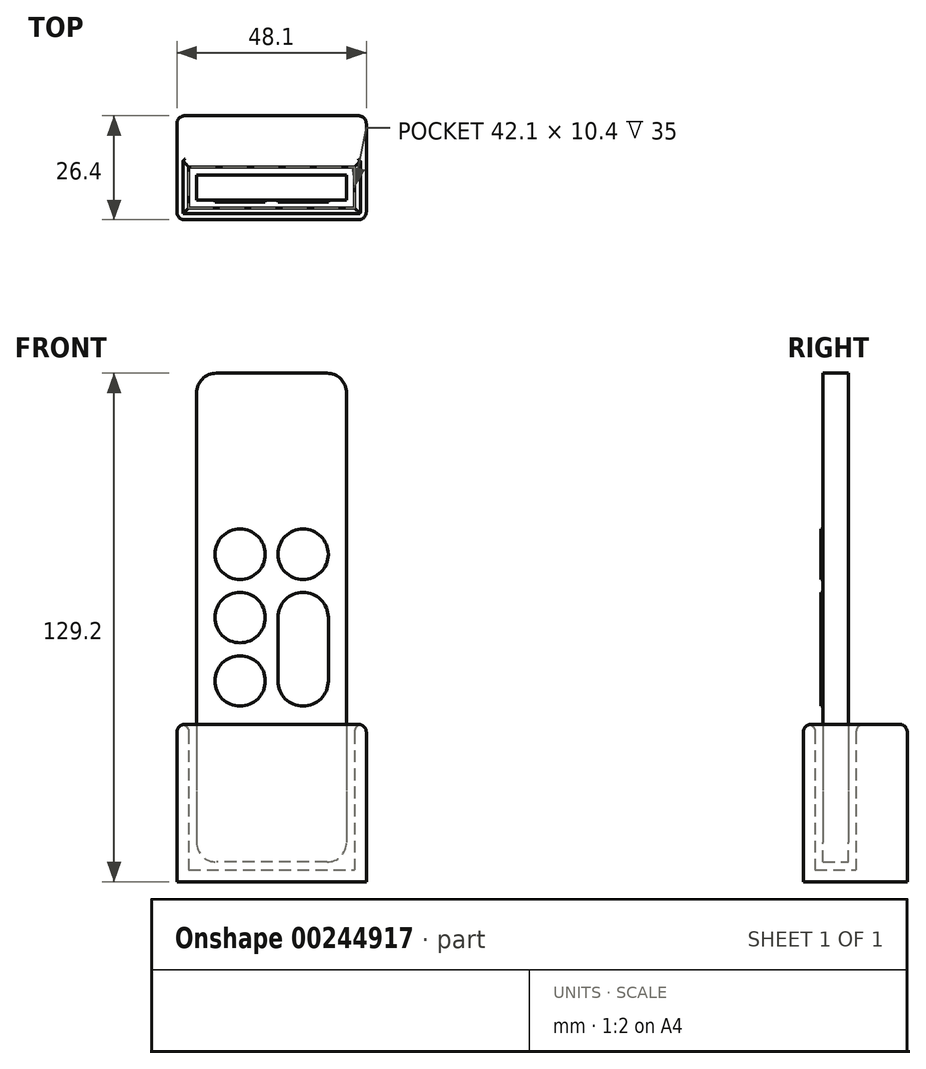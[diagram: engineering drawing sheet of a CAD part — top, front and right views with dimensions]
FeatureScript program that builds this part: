
annotation { "Feature Type Name" : "Feature", "Feature Type Description" : "" }
export const myFeature = defineFeature(function(context is Context, id is Id, definition is map)
    precondition{}
    {
        {
            var Q0;
            Q0=qCreatedBy(makeId("Front.planeOp"),FACE);
            var sketch = newSketch(context, id + "F0", { "sketchPlane" : qUnion([Q0])});
            skLineSegment(sketch, "E0.bottom", {"start": v(14.05, 62.1) * mm, "end": v(-14.05, 62.1) * mm});
            skLineSegment(sketch, "E0.top", {"start": v(14.05, -62.1) * mm, "end": v(-14.05, -62.1) * mm});
            skLineSegment(sketch, "E0.left", {"start": v(19.05, 57.1) * mm, "end": v(19.05, -57.1) * mm});
            skLineSegment(sketch, "E0.right", {"start": v(-19.05, 57.1) * mm, "end": v(-19.05, -57.1) * mm});
            skPoint(sketch, "E0.middle", {"position": v(0, 0) * mm});
            skPoint(sketch, "E1.visualSharp", {"position": v(19.05, 62.1) * mm});
            skArc(sketch, "E1.filletArc", {"start": v(19.05, 57.1) * mm, "mid": v(17.59, 60.64) * mm, "end": v(14.05, 62.1) * mm});
            skPoint(sketch, "E2.visualSharp", {"position": v(19.05, -62.1) * mm});
            skArc(sketch, "E2.filletArc", {"start": v(14.05, -62.1) * mm, "mid": v(17.59, -60.64) * mm, "end": v(19.05, -57.1) * mm});
            skPoint(sketch, "E3.visualSharp", {"position": v(-19.05, -62.1) * mm});
            skArc(sketch, "E3.filletArc", {"start": v(-19.05, -57.1) * mm, "mid": v(-17.59, -60.64) * mm, "end": v(-14.05, -62.1) * mm});
            skPoint(sketch, "E4.visualSharp", {"position": v(-19.05, 62.1) * mm});
            skArc(sketch, "E4.filletArc", {"start": v(-14.05, 62.1) * mm, "mid": v(-17.59, 60.64) * mm, "end": v(-19.05, 57.1) * mm});
            skSolve(sketch);
        }
        {
            var Q0;
            Q0 = qSketchRegion(id + "F0", true);
            extrude(context, id + "F1", {"entities" : qUnion([Q0]), "depth" : 6.4 * mm});
        }
        {
            var Q0;
            Q0=makeQuery(id+"F1.opExtrude","CAP_FACE",FACE,{"disambiguationData":[OSD([sQuery(id+"F0.wireOp",EDGE,"E0.bottom"),sQuery(id+"F0.wireOp",EDGE,"E0.top"),sQuery(id+"F0.wireOp",EDGE,"E0.left"),sQuery(id+"F0.wireOp",EDGE,"E0.right"),sQuery(id+"F0.wireOp",EDGE,"E1.filletArc"),sQuery(id+"F0.wireOp",EDGE,"E2.filletArc"),sQuery(id+"F0.wireOp",EDGE,"E3.filletArc"),sQuery(id+"F0.wireOp",EDGE,"E4.filletArc")])],"isStart":false});
            var sketch = newSketch(context, id + "F2", { "sketchPlane" : qUnion([Q0])});
            skLineSegment(sketch, "E5", {"start": v(0, 62.1) * mm, "end": v(0, -62.1) * mm, "construction": true});
            skLineSegment(sketch, "E6", {"start": v(8, 62.1) * mm, "end": v(8, -62.1) * mm, "construction": true});
            skLineSegment(sketch, "E7", {"start": v(-19.05, 0) * mm, "end": v(19.05, 0) * mm, "construction": true});
            skLineSegment(sketch, "E8", {"start": v(-19.05, 16.1) * mm, "end": v(19.05, 16.1) * mm, "construction": true});
            skCircle(sketch, "E9", {"center": v(8, 0) * mm, "radius": 6.4 * mm});
            skCircle(sketch, "E10", {"center": v(8, 16.1) * mm, "radius": 6.4 * mm});
            skCircle(sketch, "E11.MirrorC", {"center": v(8, -16.1) * mm, "radius": 6.4 * mm});
            skCircle(sketch, "E12.MirrorC", {"center": v(-8, 16.1) * mm, "radius": 6.4 * mm});
            skCircle(sketch, "E13.MirrorC", {"center": v(-8, 0) * mm, "radius": 6.4 * mm});
            skCircle(sketch, "E14.MirrorC", {"center": v(-8, -16.1) * mm, "radius": 6.4 * mm});
            skLineSegment(sketch, "E15", {"start": v(1.6, 0) * mm, "end": v(1.6, -16.1) * mm});
            skLineSegment(sketch, "E16", {"start": v(14.4, 0) * mm, "end": v(14.4, -16.1) * mm});
            skSolve(sketch);
        }
        {
            var Q0;
            Q0 = qSketchRegion(id + "F2", true);
            extrude(context, id + "F3", {"entities" : qUnion([Q0]), "operationType" : NewBodyOperationType.ADD, "depth" : .5 * mm});
        }
        {
            var Q0;
            Q0=makeQuery(id+"F1.opExtrude","SWEPT_FACE",FACE,{"disambiguationData":[OSD([sQuery(id+"F0.wireOp",EDGE,"E0.top")])]});
            var sketch = newSketch(context, id + "F4", { "sketchPlane" : qUnion([Q0])});
            skLineSegment(sketch, "E17.0", {"start": v(-24.05, 11.4) * mm, "end": v(-14.05, 11.4) * mm});
            skLineSegment(sketch, "E17.1", {"start": v(14.05, 11.4) * mm, "end": v(-14.05, 11.4) * mm});
            skLineSegment(sketch, "E17.2", {"start": v(-24.05, 11.4) * mm, "end": v(-24.05, -5) * mm});
            skLineSegment(sketch, "E17.3", {"start": v(14.05, 11.4) * mm, "end": v(24.05, 11.4) * mm});
            skLineSegment(sketch, "E17.4", {"start": v(-24.05, -5) * mm, "end": v(-14.05, -5) * mm});
            skLineSegment(sketch, "E17.5", {"start": v(14.05, -5) * mm, "end": v(-14.05, -5) * mm});
            skLineSegment(sketch, "E17.6", {"start": v(14.05, -5) * mm, "end": v(24.05, -5) * mm});
            skLineSegment(sketch, "E17.7", {"start": v(24.05, 11.4) * mm, "end": v(24.05, -5) * mm});
            skSolve(sketch);
        }
        {
            var Q0;
            Q0 = qSketchRegion(id + "F4", true);
            extrude(context, id + "F5", {"entities" : qUnion([Q0]), "oppositeDirection" : true, "depth" : 35 * mm, "hasSecondDirection" : true, "secondDirectionOppositeDirection" : false, "secondDirectionDepth" : 5 * mm});
        }
        {
            var Q0;
            Q0=makeQuery(id+"F5.opExtrude","CAP_FACE",FACE,{"disambiguationData":[OSD([sQuery(id+"F4.wireOp",EDGE,"E17.0"),sQuery(id+"F4.wireOp",EDGE,"E17.1"),sQuery(id+"F4.wireOp",EDGE,"E17.2"),sQuery(id+"F4.wireOp",EDGE,"E17.3"),sQuery(id+"F4.wireOp",EDGE,"E17.4"),sQuery(id+"F4.wireOp",EDGE,"E17.5"),sQuery(id+"F4.wireOp",EDGE,"E17.6"),sQuery(id+"F4.wireOp",EDGE,"E17.7")])],"isStart":false});
            shell(context, id + "F6", {"entities" : qUnion([Q0]), "thickness" : 3 * mm});
        }
        {
            var Q0;
            Q0=makeQuery(id+"F5.opExtrude","SWEPT_FACE",FACE,{"disambiguationData":[OSD([sQuery(id+"F4.wireOp",EDGE,"E17.4"),sQuery(id+"F4.wireOp",EDGE,"E17.5"),sQuery(id+"F4.wireOp",EDGE,"E17.6")])]});
            var sketch = newSketch(context, id + "F7", { "sketchPlane" : qUnion([Q0])});
            skSolve(sketch);
        }
        {
            var Q0;
            {var subQ0=sQuery(id+"F4.wireOp",EDGE,"E17.4");Q0=makeQuery(id+"F7.imprint","IMPRINT",FACE,{"disambiguationData":[TD([[makeQuery(id+"F7.imprint","IMPRINT",EDGE,{"derivedFrom":makeQuery(id+"F5.opExtrude","SWEPT_EDGE",EDGE,{"disambiguationData":[OSD([sQuery(id+"F4.wireOp",EDGE,"E17.2"),subQ0])]})}),-1.0]])]});}
            extrude(context, id + "F8", {"entities" : qUnion([Q0]), "operationType" : NewBodyOperationType.ADD, "depth" : 10 * mm});
        }
        {
            var Q0;
            {var subQ0=sQuery(id+"F4.wireOp",EDGE,"E17.6");var subQ1=sQuery(id+"F4.wireOp",EDGE,"E17.5");var subQ2=sQuery(id+"F4.wireOp",EDGE,"E17.4");Q0=makeQuery(id+"F8.boolean.opBoolean","MERGE",FACE,{"derivedFrom":[makeQuery(id+"F5.opExtrude","CAP_FACE",FACE,{"disambiguationData":[OSD([sQuery(id+"F4.wireOp",EDGE,"E17.0"),sQuery(id+"F4.wireOp",EDGE,"E17.1"),sQuery(id+"F4.wireOp",EDGE,"E17.2"),sQuery(id+"F4.wireOp",EDGE,"E17.3"),subQ2,subQ1,subQ0,sQuery(id+"F4.wireOp",EDGE,"E17.7")])],"isStart":false}),makeQuery(id+"F8.opExtrude","SWEPT_FACE",FACE,{"disambiguationData":[OSD([subQ2,subQ1,subQ0]),TDD([makeQuery(id+"F7.imprint","IMPRINT",EDGE,{"derivedFrom":makeQuery(id+"F5.opExtrude","CAP_EDGE",EDGE,{"disambiguationData":[OSD([subQ2,subQ1,subQ0])],"isStart":false})})])]})]});}
            var Q1;
            Q1=makeQuery(id+"F5.opExtrude","SWEPT_EDGE",EDGE,{"disambiguationData":[OSD([sQuery(id+"F4.wireOp",EDGE,"E17.3"),sQuery(id+"F4.wireOp",EDGE,"E17.7")])]});
            var Q2;
            Q2=makeQuery(id+"F8.opExtrude","CAP_EDGE",EDGE,{"disambiguationData":[OSD([sQuery(id+"F4.wireOp",EDGE,"E17.6"),sQuery(id+"F4.wireOp",EDGE,"E17.7")])],"isStart":false});
            var Q3;
            Q3=makeQuery(id+"F8.opExtrude","CAP_EDGE",EDGE,{"disambiguationData":[OSD([sQuery(id+"F4.wireOp",EDGE,"E17.2"),sQuery(id+"F4.wireOp",EDGE,"E17.4")])],"isStart":false});
            var Q4;
            Q4=makeQuery(id+"F5.opExtrude","SWEPT_EDGE",EDGE,{"disambiguationData":[OSD([sQuery(id+"F4.wireOp",EDGE,"E17.0"),sQuery(id+"F4.wireOp",EDGE,"E17.2")])]});
            fillet(context, id + "F9", {"entities" : qUnion([Q0, Q1, Q2, Q3, Q4]), "radius" : 2 * mm, "tangentPropagation" : true, "allowEdgeOverflow" : false});
        }
    });
